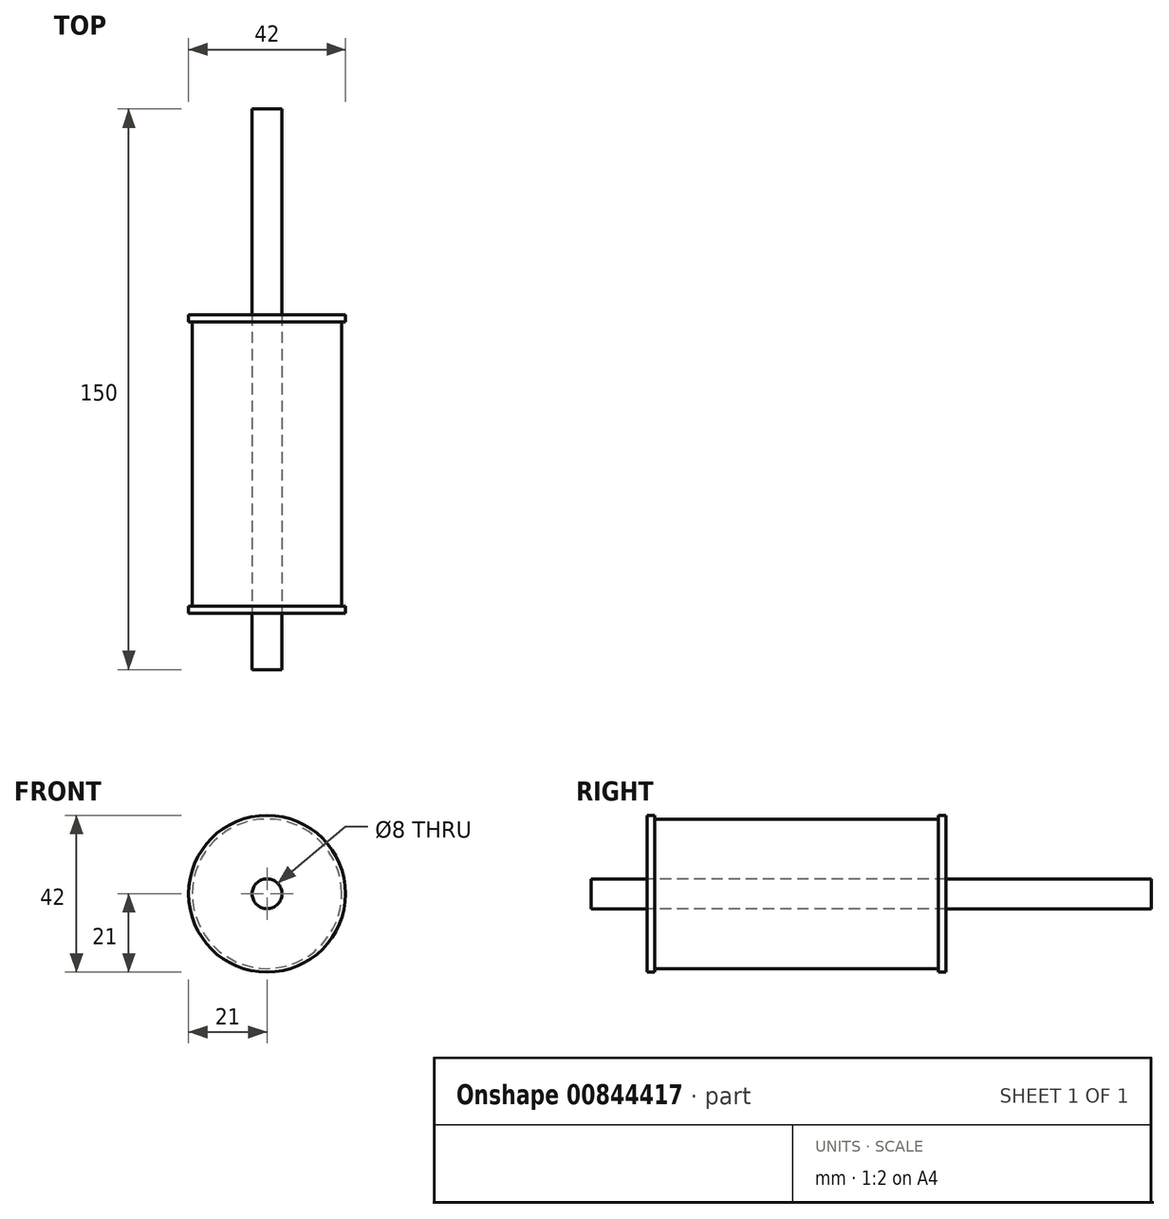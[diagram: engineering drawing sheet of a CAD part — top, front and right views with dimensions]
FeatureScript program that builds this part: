
annotation { "Feature Type Name" : "Feature", "Feature Type Description" : "" }
export const myFeature = defineFeature(function(context is Context, id is Id, definition is map)
    precondition{}
    {
        {
            var Q0;
            Q0=qCreatedBy(makeId("Front.planeOp"),FACE);
            var sketch = newSketch(context, id + "F0", { "sketchPlane" : qUnion([Q0])});
            skCircle(sketch, "E0", {"center": v(0, 0) * mm, "radius": 20 * mm});
            skCircle(sketch, "E1", {"center": v(0, 0) * mm, "radius": 21 * mm});
            skCircle(sketch, "E2", {"center": v(0, 0) * mm, "radius": 4 * mm});
            skSolve(sketch);
        }
        {
            var Q0;
            Q0=makeQuery(id+"F0.imprint","IMPRINT",FACE,{"disambiguationData":[TD([[makeQuery(id+"F0.imprint","IMPRINT",EDGE,{"derivedFrom":sQuery(id+"F0.wireOp",EDGE,"E0")}),-1.0]])]});
            var Q1;
            Q1=makeQuery(id+"F0.imprint","IMPRINT",FACE,{"disambiguationData":[TD([[makeQuery(id+"F0.imprint","IMPRINT",EDGE,{"derivedFrom":sQuery(id+"F0.wireOp",EDGE,"E0")}),1.0]])]});
            extrude(context, id + "F1", {"entities" : qUnion([Q0, Q1]), "depth" : 80 * mm, "offsetDistance" : 25 * mm, "symmetric" : true});
        }
        {
            var Q0;
            Q0=makeQuery(id+"F0.imprint","IMPRINT",FACE,{"disambiguationData":[TD([[makeQuery(id+"F0.imprint","IMPRINT",EDGE,{"derivedFrom":sQuery(id+"F0.wireOp",EDGE,"E0")}),-1.0]])]});
            extrude(context, id + "F2", {"entities" : qUnion([Q0]), "operationType" : NewBodyOperationType.REMOVE, "depth" : 76 * mm, "offsetDistance" : 25 * mm, "symmetric" : true});
        }
        {
            var Q0;
            Q0=makeQuery(id+"F1.opExtrude","CAP_FACE",FACE,{"disambiguationData":[OSD([sQuery(id+"F0.wireOp",EDGE,"E1"),sQuery(id+"F0.wireOp",EDGE,"E2")])],"isStart":false});
            cPlane(context, id + "F3", {"entities" : qUnion([Q0]), "cplaneType" : CPlaneType.OFFSET, "offset" : 15 * mm, "width" : 150 * mm, "height" : 150 * mm});
        }
        {
            var Q0;
            Q0=qCreatedBy(id+"F3.planeOp",FACE);
            var sketch = newSketch(context, id + "F4", { "sketchPlane" : qUnion([Q0])});
            skCircle(sketch, "E3", {"center": v(0, 0) * mm, "radius": 4 * mm});
            skSolve(sketch);
        }
        {
            var Q0;
            Q0=makeQuery(id+"F4.imprint","IMPRINT",FACE,{"disambiguationData":[TD([[makeQuery(id+"F4.imprint","IMPRINT",EDGE,{"derivedFrom":sQuery(id+"F4.wireOp",EDGE,"E3")}),1.0]])]});
            extrude(context, id + "F5", {"entities" : qUnion([Q0]), "oppositeDirection" : true, "depth" : 150 * mm, "offsetDistance" : 25 * mm});
        }
    });
